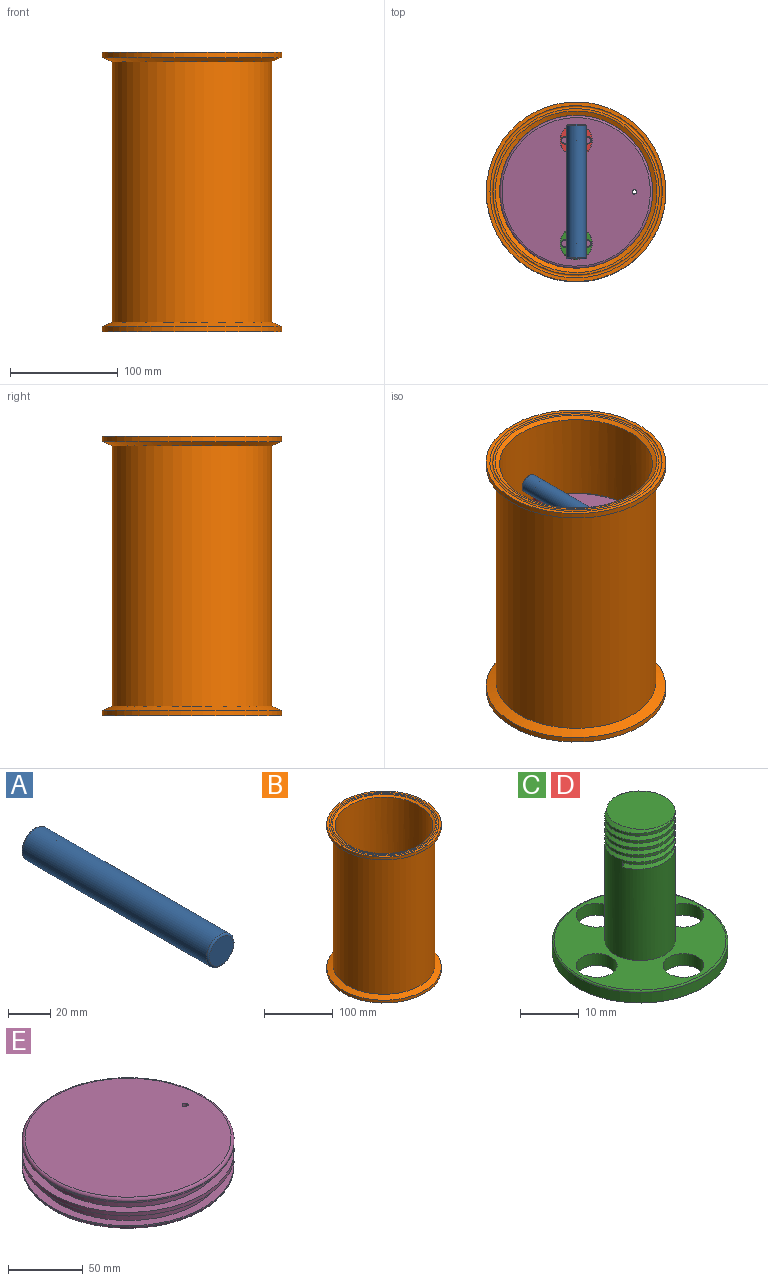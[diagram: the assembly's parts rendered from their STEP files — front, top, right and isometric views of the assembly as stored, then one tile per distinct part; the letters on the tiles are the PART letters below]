
ASSEMBLY  parts=5 mates=4
PART A: 9 faces, bbox 19.5x125x19.5 mm
  f0: cylinder r=9mm len=123mm, axis (0,1,0), area 6714mm2, adj f3,f4,f5,f6
  f1: plane 16x16mm, normal (0,-1,0), area 201.1mm2, adj f6
  f2: plane 16x16mm, normal (0,1,0), area 201.1mm2, adj f5
  f3: cylinder r=6mm len=14.29mm, axis (0,0,1), area 497.2mm2, adj f0,f8
  f4: cylinder r=6mm len=14.29mm, axis (0,0,1), area 497.2mm2, adj f0,f7
  f5: torus R=8mm, axis (0,-1,0), area 85.2mm2, adj f0,f2
  f6: torus R=8mm, axis (0,-1,0), area 85.2mm2, adj f0,f1
  f7: cone r=0mm half-angle=59deg, axis (0,0,-1), area 131.9mm2, adj f4
  f8: cone r=0mm half-angle=59deg, axis (0,0,-1), area 131.9mm2, adj f3
PART B: 13 faces, bbox 173.3x173.3x262 mm
  f0: cylinder r=71.09mm len=257.69mm, axis (0,0,-1), area 115103.1mm2, adj f11,f12
  f1: plane 154.5x154.5mm, normal (0,0,1), area 1033.8mm2, adj f2,f12
  f2: torus R=78.65mm, axis (0,0,-1), area 2173.5mm2, adj f1,f3
  f3: plane 166.9x166.9mm, normal (0,0,1), area 1746.4mm2, adj f2,f4
  f4: cylinder r=83.45mm len=166.9mm, axis (0,0,-1), area 2621.7mm2, adj f3,f5
  f5: cone r=74.09mm half-angle=67deg, axis (0,0,1), area 5033mm2, adj f4,f6
  f6: cylinder r=74.09mm len=242.05mm, axis (0,0,-1), area 112678.9mm2, adj f5,f7
  f7: cone r=74.09mm half-angle=67deg, axis (0,0,-1), area 5033mm2, adj f6,f8
  f8: cylinder r=83.45mm len=166.9mm, axis (0,0,-1), area 2621.7mm2, adj f7,f9
  f9: plane 166.9x166.9mm, normal (0,0,-1), area 1746.4mm2, adj f8,f10
  f10: torus R=78.65mm, axis (0,0,-1), area 2173.5mm2, adj f9,f11
  f11: plane 154.5x154.5mm, normal (0,0,-1), area 2870.7mm2, adj f0,f10
  f12: cone r=75.09mm half-angle=60deg, axis (0,0,1), area 2121.1mm2, adj f0,f1
PART C: 18 faces, bbox 32.9x32.9x30.6 mm
  f0: cylinder r=6mm len=20.5mm, axis (0,0,-1), area 744.6mm2, adj f1,f7,f15,f16
  f1: cylinder r=6mm len=12mm, axis (0,0,-1), area 21.2mm2, adj f0,f2,f16,f17
  f2: cylinder r=6mm len=12mm, axis (0,0,-1), area 21.2mm2, adj f1,f3,f16,f17
  f3: cylinder r=6mm len=12mm, axis (0,0,-1), area 21.2mm2, adj f2,f4,f16,f17
  f4: cylinder r=6mm len=12mm, axis (0,0,-1), area 21.2mm2, adj f3,f5,f16,f17
  f5: cylinder r=6mm len=12mm, axis (0,0,-1), area 11.1mm2, adj f4,f9,f16,f17
  f6: cylinder r=15mm len=30mm, axis (0,0,-1), area 207.3mm2, adj f8,f14
  f7: plane 29.4x29.4mm, normal (0,0,1), area 411.8mm2, adj f0,f10,f11,f12,f13,f14
  f8: plane 30x30mm, normal (0,0,-1), area 552.9mm2, adj f6,f10,f11,f12,f13
  f9: plane 12.14x11.82mm, normal (0,0,1), area 104mm2, adj f5,f16,f17
  f10: cylinder r=3.5mm len=7mm, axis (0,0,1), area 55mm2, adj f7,f8
  f11: cylinder r=3.5mm len=7mm, axis (0,0,1), area 55mm2, adj f7,f8
  f12: cylinder r=3.5mm len=7mm, axis (0,0,1), area 55mm2, adj f7,f8
  f13: cylinder r=3.5mm len=7mm, axis (0,0,1), area 55mm2, adj f7,f8
  f14: torus R=14.7mm, axis (0,0,1), area 44.1mm2, adj f6,f7
  f15: plane 0.94x0.78mm, normal (0.26,-0.97,0), area 0.4mm2, adj f0,f16,f17
  f16: bspline ~13.38x13.38mm, area 170.9mm2, adj f0,f1,f2,f3,f4,f5,f9,f15
  f17: bspline ~13.38x13.38mm, area 160.3mm2, adj f1,f2,f3,f4,f5,f9,f15,f16
PART D: same geometry as C
PART E: 30 faces, bbox 153.7x153.7x25 mm
  f0: plane 138x138mm, normal (0,0,-1), area 14718.4mm2, adj f12,f13,f14,f16,f18,f20,f22,f24
  f1: plane 138x138mm, normal (0,0,1), area 14944.8mm2, adj f2,f13
  f2: torus R=69mm, axis (0,0,1), area 1365.4mm2, adj f1,f3
  f3: cylinder r=71mm len=142mm, axis (0,0,1), area 467.8mm2, adj f2,f4
  f4: plane 142x142mm, normal (0,0,-1), area 2604.3mm2, adj f3,f5
  f5: cylinder r=64.9mm len=129.8mm, axis (0,0,1), area 3262.2mm2, adj f4,f6
  f6: plane 142x142mm, normal (0,0,1), area 2604.3mm2, adj f5,f7
  f7: cylinder r=71mm len=142mm, axis (0,0,1), area 1338.3mm2, adj f6,f8
  f8: plane 142x142mm, normal (0,0,-1), area 2604.3mm2, adj f7,f9
  f9: cylinder r=64.9mm len=129.8mm, axis (0,0,1), area 3262.2mm2, adj f8,f10
  f10: plane 142x142mm, normal (0,0,1), area 2604.3mm2, adj f9,f11
  f11: cylinder r=71mm len=142mm, axis (0,0,1), area 446.1mm2, adj f10,f12
  f12: torus R=69mm, axis (0,0,1), area 1387.1mm2, adj f0,f11
  f13: cylinder r=2mm len=25mm, axis (0,0,-1), area 314.2mm2, adj f0,f1
  f14: cylinder r=3mm len=12mm, axis (0,0,-1), area 226.2mm2, adj f0,f15
  f15: plane 6x6mm, normal (0,0,-1), area 28.3mm2, adj f14
  f16: cylinder r=3mm len=12mm, axis (0,0,-1), area 226.2mm2, adj f0,f17
  f17: plane 6x6mm, normal (0,0,-1), area 28.3mm2, adj f16
  f18: cylinder r=3mm len=12mm, axis (0,0,-1), area 226.2mm2, adj f0,f19
  f19: plane 6x6mm, normal (0,0,-1), area 28.3mm2, adj f18
  f20: cylinder r=3mm len=12mm, axis (0,0,-1), area 226.2mm2, adj f0,f21
  f21: plane 6x6mm, normal (0,0,-1), area 28.3mm2, adj f20
  f22: cylinder r=3mm len=12mm, axis (0,0,-1), area 226.2mm2, adj f0,f23
  f23: plane 6x6mm, normal (0,0,-1), area 28.3mm2, adj f22
  f24: cylinder r=3mm len=12mm, axis (0,0,-1), area 226.2mm2, adj f0,f25
  f25: plane 6x6mm, normal (0,0,-1), area 28.3mm2, adj f24
  f26: cylinder r=3mm len=12mm, axis (0,0,-1), area 226.2mm2, adj f0,f27
  f27: plane 6x6mm, normal (0,0,-1), area 28.3mm2, adj f26
  f28: cylinder r=3mm len=12mm, axis (0,0,-1), area 226.2mm2, adj f0,f29
  f29: plane 6x6mm, normal (0,0,-1), area 28.3mm2, adj f28
PLACE A t=(105.94,45.37,50.78)mm
PLACE B t=(105.56,45.23,-151.9)mm fixed
PLACE C t=(105.61,-2.77,21.57)mm
PLACE D t=(105.61,93.23,21.57)mm
PLACE E rot(axis=(1,0,0),180deg) t=(105.61,45.23,-3.43)mm
MATE slider E.f1 <-> B.f0  axis (0,0,-1) through (105.56,45.23,-3.43)mm
MATE fastened D.f9 <-> A.f4  axis (0,0,1) through (105.94,93.37,51.07)mm
MATE fastened E.f26 <-> C.f10  axis (0,0,1) through (105.61,-13.27,21.57)mm
MATE fastened C.f9 <-> A.f3  axis (0,0,1) through (105.94,-2.63,51.07)mm
